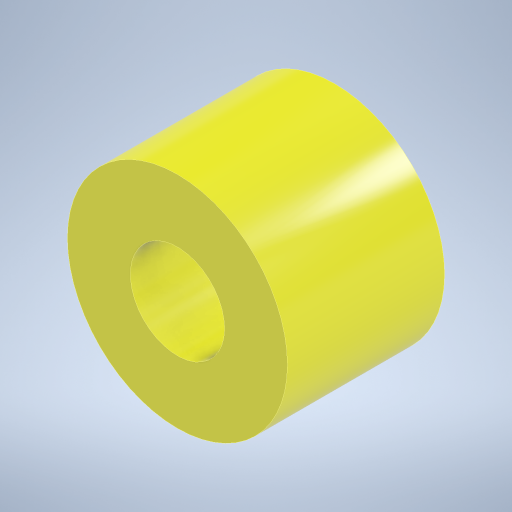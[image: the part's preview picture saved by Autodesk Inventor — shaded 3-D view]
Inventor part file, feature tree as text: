
AUTODESK INVENTOR PART (.ipt)
format: ipt  version: 2023.1 (Build 271208000, 208)  size: 222,720 bytes
history: native  units: mm
features: extrude x1, sketch x1
ambient origin geometry x8: Origin, YZ Plane, XZ Plane, XY Plane, X Axis, Y Axis, Z Axis, Center Point
bodies: Solid1 (feature_tree)
feature tree (2):
  extrude  "Extrusion1"  Depth=5.0mm
  sketch  "Sketch1"  dims[d0=3.0mm d1=7.0mm d2=5.0mm d3=0.0mm]
